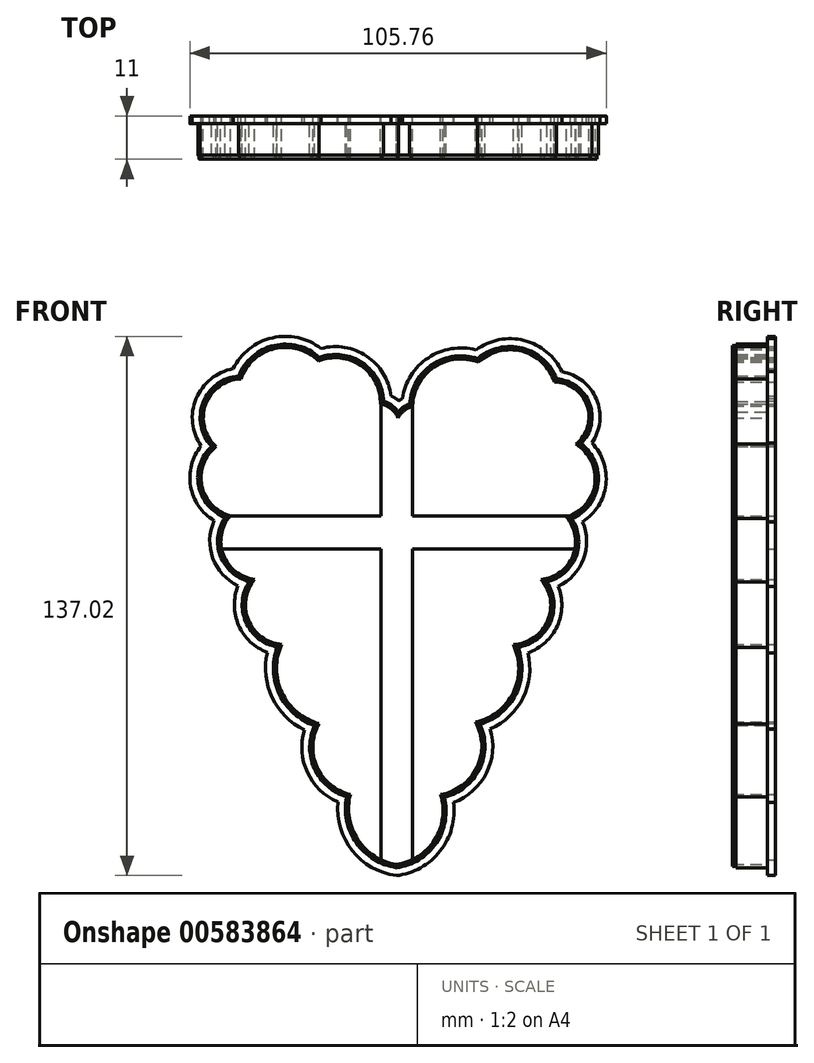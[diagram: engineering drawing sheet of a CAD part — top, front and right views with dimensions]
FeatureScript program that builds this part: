
annotation { "Feature Type Name" : "Feature", "Feature Type Description" : "" }
export const myFeature = defineFeature(function(context is Context, id is Id, definition is map)
    precondition{}
    {
        {
            var Q0;
            Q0=qCreatedBy(makeId("Front.planeOp"),FACE);
            var sketch = newSketch(context, id + "F0", { "sketchPlane" : qUnion([Q0])});
            skArc(sketch, "E0", {"start": v(-2.57, 36.41) * mm, "mid": v(-7.48, 46.12) * mm, "end": v(-18.29, 47.33) * mm});
            skPoint(sketch, "E0.first.point", {"position": v(-18.29, 47.33) * mm});
            skPoint(sketch, "E0.second.point", {"position": v(-7.66, 46.24) * mm});
            skPoint(sketch, "E0.third.point", {"position": v(-2.57, 37.02) * mm});
            skArc(sketch, "E1", {"start": v(-18.29, 47.33) * mm, "mid": v(-29.42, 50.48) * mm, "end": v(-38.03, 42.75) * mm});
            skPoint(sketch, "E1.first.point", {"position": v(-38.03, 42.75) * mm});
            skPoint(sketch, "E1.second.point", {"position": v(-28.67, 50.63) * mm});
            skArc(sketch, "E2", {"start": v(-38.03, 42.75) * mm, "mid": v(-46.97, 36.29) * mm, "end": v(-44.33, 25.58) * mm});
            skPoint(sketch, "E2.second.point", {"position": v(-44.33, 25.58) * mm});
            skPoint(sketch, "E2.third.point", {"position": v(-47.27, 35.29) * mm});
            skArc(sketch, "E3", {"start": v(-44.33, 25.58) * mm, "mid": v(-47.96, 15.67) * mm, "end": v(-40.7, 8) * mm});
            skPoint(sketch, "E3.first.point", {"position": v(-40.7, 8) * mm});
            skPoint(sketch, "E3.third.point", {"position": v(-48, 15.92) * mm});
            skArc(sketch, "E4", {"start": v(1.87, 32.88) * mm, "mid": v(0.1, 35.21) * mm, "end": v(-2.57, 36.41) * mm});
            skPoint(sketch, "E4.first.point", {"position": v(-2.57, 36.41) * mm});
            skPoint(sketch, "E4.second.point", {"position": v(1.39, 33.8) * mm});
            skPoint(sketch, "E4.third.point", {"position": v(0, 35.29) * mm});
            skArc(sketch, "E5", {"start": v(5.63, 35.85) * mm, "mid": v(3.47, 34.72) * mm, "end": v(1.87, 32.88) * mm});
            skPoint(sketch, "E5.first.point", {"position": v(1.87, 32.88) * mm});
            skPoint(sketch, "E5.second.point", {"position": v(5.63, 35.85) * mm});
            skPoint(sketch, "E5.third.point", {"position": v(3.98, 35.09) * mm});
            skPoint(sketch, "E6.second.point", {"position": v(22.32, 47.02) * mm});
            skPoint(sketch, "E6.third.point", {"position": v(11.44, 46) * mm});
            skArc(sketch, "E7", {"start": v(41.61, 41.97) * mm, "mid": v(33.35, 49.8) * mm, "end": v(22.32, 47.02) * mm});
            skPoint(sketch, "E7.second.point", {"position": v(41.61, 41.97) * mm});
            skPoint(sketch, "E7.third.point", {"position": v(33.4, 49.78) * mm});
            skPoint(sketch, "E8.second.point", {"position": v(47.09, 26.2) * mm});
            skPoint(sketch, "E8.third.point", {"position": v(50.14, 35.85) * mm});
            skArc(sketch, "E9", {"start": v(44.73, 7.66) * mm, "mid": v(51.92, 16.16) * mm, "end": v(47.09, 26.2) * mm});
            skPoint(sketch, "E9.first.point", {"position": v(44.73, 7.66) * mm});
            skPoint(sketch, "E9.third.point", {"position": v(52, 17.18) * mm});
            skArc(sketch, "E10", {"start": v(38.28, -8.2) * mm, "mid": v(46.3, -2.23) * mm, "end": v(44.73, 7.66) * mm});
            skPoint(sketch, "E10.first.point", {"position": v(38.28, -8.2) * mm});
            skPoint(sketch, "E10.third.point", {"position": v(46, -2.91) * mm});
            skArc(sketch, "E11", {"start": v(31.17, -24.73) * mm, "mid": v(39.9, -18.7) * mm, "end": v(38.28, -8.2) * mm});
            skPoint(sketch, "E11.first.point", {"position": v(31.17, -24.73) * mm});
            skPoint(sketch, "E11.third.point", {"position": v(39.57, -19.38) * mm});
            skArc(sketch, "E12", {"start": v(21.57, -44.41) * mm, "mid": v(31.18, -36.92) * mm, "end": v(31.17, -24.73) * mm});
            skPoint(sketch, "E12.first.point", {"position": v(22.32, -44.23) * mm});
            skPoint(sketch, "E12.third.point", {"position": v(30.6, -38) * mm});
            skPoint(sketch, "E13.first.point", {"position": v(12.68, -62.83) * mm});
            skPoint(sketch, "E13.second.point", {"position": v(21.57, -44.41) * mm});
            skPoint(sketch, "E13.third.point", {"position": v(22.12, -55.51) * mm});
            skArc(sketch, "E14", {"start": v(1.5, -80.6) * mm, "mid": v(11.22, -74.32) * mm, "end": v(12.68, -62.83) * mm});
            skPoint(sketch, "E14.first.point", {"position": v(1.5, -80.6) * mm});
            skPoint(sketch, "E14.third.point", {"position": v(11.36, -74.1) * mm});
            skArc(sketch, "E15", {"start": v(-10.23, -62.83) * mm, "mid": v(-8.29, -74.3) * mm, "end": v(1.5, -80.6) * mm});
            skPoint(sketch, "E15.first.point", {"position": v(-10.23, -62.83) * mm});
            skPoint(sketch, "E15.third.point", {"position": v(-7.85, -74.93) * mm});
            skArc(sketch, "E16", {"start": v(-18.2, -44.81) * mm, "mid": v(-18.68, -55.8) * mm, "end": v(-10.23, -62.83) * mm});
            skPoint(sketch, "E16.second.point", {"position": v(-18.2, -44.81) * mm});
            skPoint(sketch, "E16.third.point", {"position": v(-18.8, -55.51) * mm});
            skArc(sketch, "E17", {"start": v(-40.7, 8) * mm, "mid": v(-42.48, -1.95) * mm, "end": v(-34.5, -8.14) * mm});
            skPoint(sketch, "E17.second.point", {"position": v(-34.5, -8.14) * mm});
            skPoint(sketch, "E17.third.point", {"position": v(-42.41, -2.11) * mm});
            skArc(sketch, "E18", {"start": v(-34.5, -8.14) * mm, "mid": v(-36.12, -18.5) * mm, "end": v(-27.65, -24.68) * mm});
            skPoint(sketch, "E18.second.point", {"position": v(-27.65, -24.68) * mm});
            skPoint(sketch, "E18.third.point", {"position": v(-35.78, -19.23) * mm});
            skArc(sketch, "E19", {"start": v(-27.65, -24.68) * mm, "mid": v(-27.57, -36.93) * mm, "end": v(-18.2, -44.81) * mm});
            skPoint(sketch, "E19.third.point", {"position": v(-27.65, -36.76) * mm});
            skArc(sketch, "E20.trimOffspring", {"start": v(22.32, 47.02) * mm, "mid": v(11.07, 45.77) * mm, "end": v(5.63, 35.85) * mm});
            skArc(sketch, "E21.trimOffspring", {"start": v(47.09, 26.2) * mm, "mid": v(49.92, 36.02) * mm, "end": v(41.61, 41.97) * mm});
            skArc(sketch, "E22.trimOffspring", {"start": v(12.68, -62.83) * mm, "mid": v(21.94, -55.95) * mm, "end": v(21.57, -44.41) * mm});
            skArc(sketch, "E23.0", {"start": v(45.43, 7.45) * mm, "mid": v(52.33, 16.13) * mm, "end": v(47.79, 26.24) * mm});
            skArc(sketch, "E23.1", {"start": v(39.07, -8.52) * mm, "mid": v(46.72, -2.32) * mm, "end": v(45.43, 7.45) * mm});
            skArc(sketch, "E23.2", {"start": v(31.8, -25.1) * mm, "mid": v(40.26, -18.92) * mm, "end": v(39.07, -8.52) * mm});
            skArc(sketch, "E23.3", {"start": v(22.2, -44.7) * mm, "mid": v(31.55, -37.13) * mm, "end": v(31.8, -25.1) * mm});
            skArc(sketch, "E23.4", {"start": v(13.22, -63.16) * mm, "mid": v(22.3, -56.16) * mm, "end": v(22.2, -44.7) * mm});
            skArc(sketch, "E23.5", {"start": v(47.79, 26.24) * mm, "mid": v(50.27, 36.28) * mm, "end": v(41.92, 42.39) * mm});
            skArc(sketch, "E23.6", {"start": v(1.49, -81.03) * mm, "mid": v(11.43, -74.77) * mm, "end": v(13.22, -63.16) * mm});
            skArc(sketch, "E23.7", {"start": v(-10.73, -63.13) * mm, "mid": v(-8.5, -74.73) * mm, "end": v(1.49, -81.03) * mm});
            skArc(sketch, "E23.8", {"start": v(-18.8, -45.07) * mm, "mid": v(-19.05, -56.01) * mm, "end": v(-10.73, -63.13) * mm});
            skArc(sketch, "E23.9", {"start": v(-28.26, -25.04) * mm, "mid": v(-27.94, -37.14) * mm, "end": v(-18.8, -45.07) * mm});
            skArc(sketch, "E23.10", {"start": v(1.92, 33.72) * mm, "mid": v(0.2, 35.66) * mm, "end": v(-2.14, 36.75) * mm});
            skArc(sketch, "E23.11", {"start": v(5.22, 36.16) * mm, "mid": v(3.39, 35.19) * mm, "end": v(1.92, 33.72) * mm});
            skArc(sketch, "E23.12", {"start": v(22.22, 47.5) * mm, "mid": v(10.86, 46.13) * mm, "end": v(5.22, 36.16) * mm});
            skArc(sketch, "E23.13", {"start": v(41.92, 42.39) * mm, "mid": v(33.44, 50.2) * mm, "end": v(22.22, 47.5) * mm});
            skArc(sketch, "E23.14", {"start": v(-2.14, 36.75) * mm, "mid": v(-7.27, 46.48) * mm, "end": v(-18.19, 47.82) * mm});
            skArc(sketch, "E23.15", {"start": v(-18.19, 47.82) * mm, "mid": v(-29.51, 50.89) * mm, "end": v(-38.33, 43.15) * mm});
            skArc(sketch, "E23.16", {"start": v(-38.33, 43.15) * mm, "mid": v(-47.32, 36.52) * mm, "end": v(-44.96, 25.6) * mm});
            skArc(sketch, "E23.17", {"start": v(-44.96, 25.6) * mm, "mid": v(-48.39, 15.66) * mm, "end": v(-41.42, 7.78) * mm});
            skArc(sketch, "E23.18", {"start": v(-41.42, 7.78) * mm, "mid": v(-42.89, -2.05) * mm, "end": v(-35.27, -8.44) * mm});
            skArc(sketch, "E23.19", {"start": v(-35.27, -8.44) * mm, "mid": v(-36.48, -18.73) * mm, "end": v(-28.26, -25.04) * mm});
            skSolve(sketch);
        }
        {
            var Q0;
            Q0 = qSketchRegion(id + "F0", true);
            extrude(context, id + "F1", {"entities" : qUnion([Q0]), "depth" : 11 * mm, "offsetDistance" : 25 * mm});
        }
        {
            var Q0;
            Q0=qCreatedBy(makeId("Front.planeOp"),FACE);
            var sketch = newSketch(context, id + "F2", { "sketchPlane" : qUnion([Q0])});
            skArc(sketch, "E24.0.0", {"start": v(-10.23, -62.83) * mm, "mid": v(-8.29, -74.3) * mm, "end": v(1.5, -80.6) * mm});
            skArc(sketch, "E24.0.1", {"start": v(1.5, -80.6) * mm, "mid": v(11.22, -74.32) * mm, "end": v(12.68, -62.83) * mm});
            skArc(sketch, "E24.0.2", {"start": v(12.68, -62.83) * mm, "mid": v(21.94, -55.95) * mm, "end": v(21.57, -44.41) * mm});
            skArc(sketch, "E24.0.3", {"start": v(21.57, -44.41) * mm, "mid": v(31.18, -36.92) * mm, "end": v(31.17, -24.73) * mm});
            skArc(sketch, "E24.0.4", {"start": v(31.17, -24.73) * mm, "mid": v(39.9, -18.7) * mm, "end": v(38.28, -8.2) * mm});
            skArc(sketch, "E24.0.5", {"start": v(38.28, -8.2) * mm, "mid": v(46.3, -2.23) * mm, "end": v(44.73, 7.66) * mm});
            skArc(sketch, "E24.0.6", {"start": v(44.73, 7.66) * mm, "mid": v(51.92, 16.16) * mm, "end": v(47.09, 26.2) * mm});
            skArc(sketch, "E24.0.7", {"start": v(47.09, 26.2) * mm, "mid": v(49.92, 36.02) * mm, "end": v(41.61, 41.97) * mm});
            skArc(sketch, "E24.0.8", {"start": v(41.61, 41.97) * mm, "mid": v(33.35, 49.8) * mm, "end": v(22.32, 47.02) * mm});
            skArc(sketch, "E24.0.9", {"start": v(22.32, 47.02) * mm, "mid": v(11.07, 45.77) * mm, "end": v(5.63, 35.85) * mm});
            skArc(sketch, "E24.0.10", {"start": v(5.63, 35.85) * mm, "mid": v(3.47, 34.72) * mm, "end": v(1.87, 32.88) * mm});
            skArc(sketch, "E24.0.11", {"start": v(1.87, 32.88) * mm, "mid": v(0.1, 35.21) * mm, "end": v(-2.57, 36.41) * mm});
            skArc(sketch, "E24.0.12", {"start": v(-2.57, 36.41) * mm, "mid": v(-7.48, 46.12) * mm, "end": v(-18.29, 47.33) * mm});
            skArc(sketch, "E24.0.13", {"start": v(-18.29, 47.33) * mm, "mid": v(-29.42, 50.48) * mm, "end": v(-38.03, 42.75) * mm});
            skArc(sketch, "E24.0.14", {"start": v(-38.03, 42.75) * mm, "mid": v(-46.97, 36.29) * mm, "end": v(-44.33, 25.58) * mm});
            skArc(sketch, "E24.0.15", {"start": v(-44.33, 25.58) * mm, "mid": v(-47.96, 15.67) * mm, "end": v(-40.7, 8) * mm});
            skArc(sketch, "E24.0.16", {"start": v(-40.7, 8) * mm, "mid": v(-42.48, -1.95) * mm, "end": v(-34.5, -8.14) * mm});
            skArc(sketch, "E24.0.17", {"start": v(-34.5, -8.14) * mm, "mid": v(-36.12, -18.5) * mm, "end": v(-27.65, -24.68) * mm});
            skArc(sketch, "E24.0.18", {"start": v(-27.65, -24.68) * mm, "mid": v(-27.57, -36.93) * mm, "end": v(-18.2, -44.81) * mm});
            skArc(sketch, "E24.0.19", {"start": v(-18.2, -44.81) * mm, "mid": v(-18.68, -55.8) * mm, "end": v(-10.23, -62.83) * mm});
            skArc(sketch, "E25.0", {"start": v(-19.33, -45.3) * mm, "mid": v(-19.38, -56.2) * mm, "end": v(-11.18, -63.4) * mm});
            skArc(sketch, "E25.1", {"start": v(-28.79, -25.34) * mm, "mid": v(-28.28, -37.32) * mm, "end": v(-19.33, -45.3) * mm});
            skArc(sketch, "E25.2", {"start": v(-35.9, -8.7) * mm, "mid": v(-36.8, -18.92) * mm, "end": v(-28.79, -25.34) * mm});
            skArc(sketch, "E25.3", {"start": v(-42.03, 7.6) * mm, "mid": v(-43.25, -2.16) * mm, "end": v(-35.9, -8.7) * mm});
            skArc(sketch, "E25.4", {"start": v(-45.5, 25.63) * mm, "mid": v(-48.77, 15.64) * mm, "end": v(-42.03, 7.6) * mm});
            skArc(sketch, "E25.5", {"start": v(-11.18, -63.4) * mm, "mid": v(-8.7, -75.11) * mm, "end": v(1.48, -81.42) * mm});
            skArc(sketch, "E25.6", {"start": v(-38.6, 43.52) * mm, "mid": v(-47.65, 36.73) * mm, "end": v(-45.5, 25.63) * mm});
            skArc(sketch, "E25.7", {"start": v(-18.1, 48.25) * mm, "mid": v(-29.6, 51.26) * mm, "end": v(-38.6, 43.52) * mm});
            skArc(sketch, "E25.8", {"start": v(-1.77, 37.05) * mm, "mid": v(-7.08, 46.81) * mm, "end": v(-18.1, 48.25) * mm});
            skArc(sketch, "E25.9", {"start": v(1.96, 34.38) * mm, "mid": v(0.33, 36.04) * mm, "end": v(-1.77, 37.05) * mm});
            skArc(sketch, "E25.10", {"start": v(32.35, -25.41) * mm, "mid": v(40.59, -19.11) * mm, "end": v(39.72, -8.78) * mm});
            skArc(sketch, "E25.11", {"start": v(22.74, -44.95) * mm, "mid": v(31.88, -37.31) * mm, "end": v(32.35, -25.41) * mm});
            skArc(sketch, "E25.12", {"start": v(13.69, -63.45) * mm, "mid": v(22.63, -56.36) * mm, "end": v(22.74, -44.95) * mm});
            skArc(sketch, "E25.13", {"start": v(1.48, -81.42) * mm, "mid": v(11.62, -75.17) * mm, "end": v(13.69, -63.45) * mm});
            skArc(sketch, "E25.14", {"start": v(39.72, -8.78) * mm, "mid": v(47.1, -2.41) * mm, "end": v(46.02, 7.28) * mm});
            skArc(sketch, "E25.15", {"start": v(46.02, 7.28) * mm, "mid": v(52.71, 16.1) * mm, "end": v(48.38, 26.28) * mm});
            skArc(sketch, "E25.16", {"start": v(48.38, 26.28) * mm, "mid": v(50.6, 36.51) * mm, "end": v(42.19, 42.75) * mm});
            skArc(sketch, "E25.17", {"start": v(42.19, 42.75) * mm, "mid": v(33.52, 50.58) * mm, "end": v(22.14, 47.93) * mm});
            skArc(sketch, "E25.18", {"start": v(22.14, 47.93) * mm, "mid": v(10.66, 46.45) * mm, "end": v(4.85, 36.43) * mm});
            skArc(sketch, "E25.19", {"start": v(4.85, 36.43) * mm, "mid": v(3.28, 35.58) * mm, "end": v(1.96, 34.38) * mm});
            skSolve(sketch);
        }
        {
            var Q0;
            Q0 = qSketchRegion(id + "F2", true);
            extrude(context, id + "F3", {"entities" : qUnion([Q0]), "operationType" : NewBodyOperationType.ADD, "depth" : 10 * mm, "offsetDistance" : 25 * mm});
        }
        {
            var Q0;
            Q0=qCreatedBy(makeId("Front.planeOp"),FACE);
            var sketch = newSketch(context, id + "F4", { "sketchPlane" : qUnion([Q0])});
            skArc(sketch, "E26.0.0", {"start": v(-10.23, -62.83) * mm, "mid": v(-8.29, -74.3) * mm, "end": v(1.5, -80.6) * mm});
            skArc(sketch, "E26.0.1", {"start": v(1.5, -80.6) * mm, "mid": v(11.22, -74.32) * mm, "end": v(12.68, -62.83) * mm});
            skArc(sketch, "E26.0.2", {"start": v(12.68, -62.83) * mm, "mid": v(21.94, -55.95) * mm, "end": v(21.57, -44.41) * mm});
            skArc(sketch, "E26.0.3", {"start": v(21.57, -44.41) * mm, "mid": v(31.18, -36.92) * mm, "end": v(31.17, -24.73) * mm});
            skArc(sketch, "E26.0.4", {"start": v(31.17, -24.73) * mm, "mid": v(39.9, -18.7) * mm, "end": v(38.28, -8.2) * mm});
            skArc(sketch, "E26.0.5", {"start": v(38.28, -8.2) * mm, "mid": v(46.3, -2.23) * mm, "end": v(44.73, 7.66) * mm});
            skArc(sketch, "E26.0.6", {"start": v(44.73, 7.66) * mm, "mid": v(51.92, 16.16) * mm, "end": v(47.09, 26.2) * mm});
            skArc(sketch, "E26.0.7", {"start": v(47.09, 26.2) * mm, "mid": v(49.92, 36.02) * mm, "end": v(41.61, 41.97) * mm});
            skArc(sketch, "E26.0.8", {"start": v(41.61, 41.97) * mm, "mid": v(33.35, 49.8) * mm, "end": v(22.32, 47.02) * mm});
            skArc(sketch, "E26.0.9", {"start": v(22.32, 47.02) * mm, "mid": v(11.07, 45.77) * mm, "end": v(5.63, 35.85) * mm});
            skArc(sketch, "E26.0.10", {"start": v(5.63, 35.85) * mm, "mid": v(3.47, 34.72) * mm, "end": v(1.87, 32.88) * mm});
            skArc(sketch, "E26.0.11", {"start": v(1.87, 32.88) * mm, "mid": v(0.1, 35.21) * mm, "end": v(-2.57, 36.41) * mm});
            skArc(sketch, "E26.0.12", {"start": v(-2.57, 36.41) * mm, "mid": v(-7.48, 46.12) * mm, "end": v(-18.29, 47.33) * mm});
            skArc(sketch, "E26.0.13", {"start": v(-18.29, 47.33) * mm, "mid": v(-29.42, 50.48) * mm, "end": v(-38.03, 42.75) * mm});
            skArc(sketch, "E26.0.14", {"start": v(-38.03, 42.75) * mm, "mid": v(-46.97, 36.29) * mm, "end": v(-44.33, 25.58) * mm});
            skArc(sketch, "E26.0.15", {"start": v(-44.33, 25.58) * mm, "mid": v(-47.96, 15.67) * mm, "end": v(-40.7, 8) * mm});
            skArc(sketch, "E26.0.16", {"start": v(-40.7, 8) * mm, "mid": v(-42.48, -1.95) * mm, "end": v(-34.5, -8.14) * mm});
            skArc(sketch, "E26.0.17", {"start": v(-34.5, -8.14) * mm, "mid": v(-36.12, -18.5) * mm, "end": v(-27.65, -24.68) * mm});
            skArc(sketch, "E26.0.18", {"start": v(-27.65, -24.68) * mm, "mid": v(-27.57, -36.93) * mm, "end": v(-18.2, -44.81) * mm});
            skArc(sketch, "E26.0.19", {"start": v(-18.2, -44.81) * mm, "mid": v(-18.68, -55.8) * mm, "end": v(-10.23, -62.83) * mm});
            skArc(sketch, "E27.0", {"start": v(-21.89, -46.4) * mm, "mid": v(-21.13, -57.18) * mm, "end": v(-13.39, -64.72) * mm});
            skArc(sketch, "E27.1", {"start": v(-31.3, -26.71) * mm, "mid": v(-30.06, -38.22) * mm, "end": v(-21.89, -46.4) * mm});
            skArc(sketch, "E27.2", {"start": v(-38.73, -9.8) * mm, "mid": v(-38.6, -19.83) * mm, "end": v(-31.3, -26.71) * mm});
            skArc(sketch, "E27.3", {"start": v(-44.8, 6.74) * mm, "mid": v(-45.16, -2.77) * mm, "end": v(-38.73, -9.8) * mm});
            skArc(sketch, "E27.4", {"start": v(-48.14, 25.72) * mm, "mid": v(-50.77, 15.48) * mm, "end": v(-44.8, 6.74) * mm});
            skArc(sketch, "E27.5", {"start": v(-13.39, -64.72) * mm, "mid": v(-9.74, -77.07) * mm, "end": v(1.46, -83.43) * mm});
            skArc(sketch, "E27.6", {"start": v(-39.97, 45.35) * mm, "mid": v(-49.4, 37.76) * mm, "end": v(-48.14, 25.72) * mm});
            skArc(sketch, "E27.7", {"start": v(-17.65, 50.49) * mm, "mid": v(-30.03, 53.21) * mm, "end": v(-39.97, 45.35) * mm});
            skArc(sketch, "E27.8", {"start": v(0.13, 38.47) * mm, "mid": v(-6.03, 48.52) * mm, "end": v(-17.65, 50.49) * mm});
            skArc(sketch, "E27.9", {"start": v(2.1, 37.2) * mm, "mid": v(1.16, 37.9) * mm, "end": v(0.13, 38.47) * mm});
            skArc(sketch, "E27.10", {"start": v(34.9, -26.83) * mm, "mid": v(42.37, -20.02) * mm, "end": v(42.56, -9.9) * mm});
            skArc(sketch, "E27.11", {"start": v(25.33, -46.14) * mm, "mid": v(33.65, -38.24) * mm, "end": v(34.9, -26.83) * mm});
            skArc(sketch, "E27.12", {"start": v(15.99, -64.85) * mm, "mid": v(24.37, -57.35) * mm, "end": v(25.33, -46.14) * mm});
            skArc(sketch, "E27.13", {"start": v(1.46, -83.43) * mm, "mid": v(12.63, -77.19) * mm, "end": v(15.99, -64.85) * mm});
            skArc(sketch, "E27.14", {"start": v(42.56, -9.9) * mm, "mid": v(49, -3) * mm, "end": v(48.75, 6.45) * mm});
            skArc(sketch, "E27.15", {"start": v(48.75, 6.45) * mm, "mid": v(54.7, 15.9) * mm, "end": v(51.15, 26.5) * mm});
            skArc(sketch, "E27.16", {"start": v(51.15, 26.5) * mm, "mid": v(52.3, 37.61) * mm, "end": v(43.58, 44.6) * mm});
            skArc(sketch, "E27.17", {"start": v(43.58, 44.6) * mm, "mid": v(33.96, 52.53) * mm, "end": v(21.72, 50.15) * mm});
            skArc(sketch, "E27.18", {"start": v(21.72, 50.15) * mm, "mid": v(9.58, 48.14) * mm, "end": v(2.98, 37.75) * mm});
            skArc(sketch, "E27.19", {"start": v(2.98, 37.75) * mm, "mid": v(2.53, 37.49) * mm, "end": v(2.1, 37.2) * mm});
            skSolve(sketch);
        }
        {
            var Q0;
            Q0 = qSketchRegion(id + "F4", true);
            extrude(context, id + "F5", {"entities" : qUnion([Q0]), "operationType" : NewBodyOperationType.ADD, "depth" : 2 * mm, "offsetDistance" : 25 * mm});
        }
        {
            var Q0;
            Q0=qCreatedBy(makeId("Front.planeOp"),FACE);
            var sketch = newSketch(context, id + "F6", { "sketchPlane" : qUnion([Q0])});
            skLineSegment(sketch, "E28.left", {"start": v(-42.5, 8) * mm, "end": v(-43.88, -0.5) * mm});
            skPoint(sketch, "E29.left.start.orphan", {"position": v(-43.88, -0.5) * mm});
            skPoint(sketch, "E30.bottom.start.orphan", {"position": v(-45.25, -9) * mm});
            skLineSegment(sketch, "E31", {"start": v(-42.5, 8) * mm, "end": v(47.37, 8) * mm});
            skLineSegment(sketch, "E32", {"start": v(47.37, 8) * mm, "end": v(48.1, -0.5) * mm});
            skLineSegment(sketch, "E33", {"start": v(48.1, -0.5) * mm, "end": v(-43.88, -0.5) * mm});
            skLineSegment(sketch, "E34", {"start": v(2.24, 35.57) * mm, "end": v(5.57, 35.86) * mm});
            skLineSegment(sketch, "E35", {"start": v(5.57, 35.86) * mm, "end": v(5.57, -80.5) * mm});
            skLineSegment(sketch, "E36", {"start": v(5.57, -80.5) * mm, "end": v(0.72, -81.8) * mm});
            skLineSegment(sketch, "E37", {"start": v(0.72, -81.8) * mm, "end": v(-2.43, -80.6) * mm});
            skLineSegment(sketch, "E38", {"start": v(-2.43, -80.6) * mm, "end": v(-2.43, 36.43) * mm});
            skLineSegment(sketch, "E39", {"start": v(-2.43, 36.43) * mm, "end": v(2.24, 35.57) * mm});
            skSolve(sketch);
        }
        {
            var Q0;
            Q0 = qSketchRegion(id + "F6", true);
            extrude(context, id + "F7", {"entities" : qUnion([Q0]), "operationType" : NewBodyOperationType.ADD, "depth" : 2 * mm, "offsetDistance" : 25 * mm});
        }
    });
